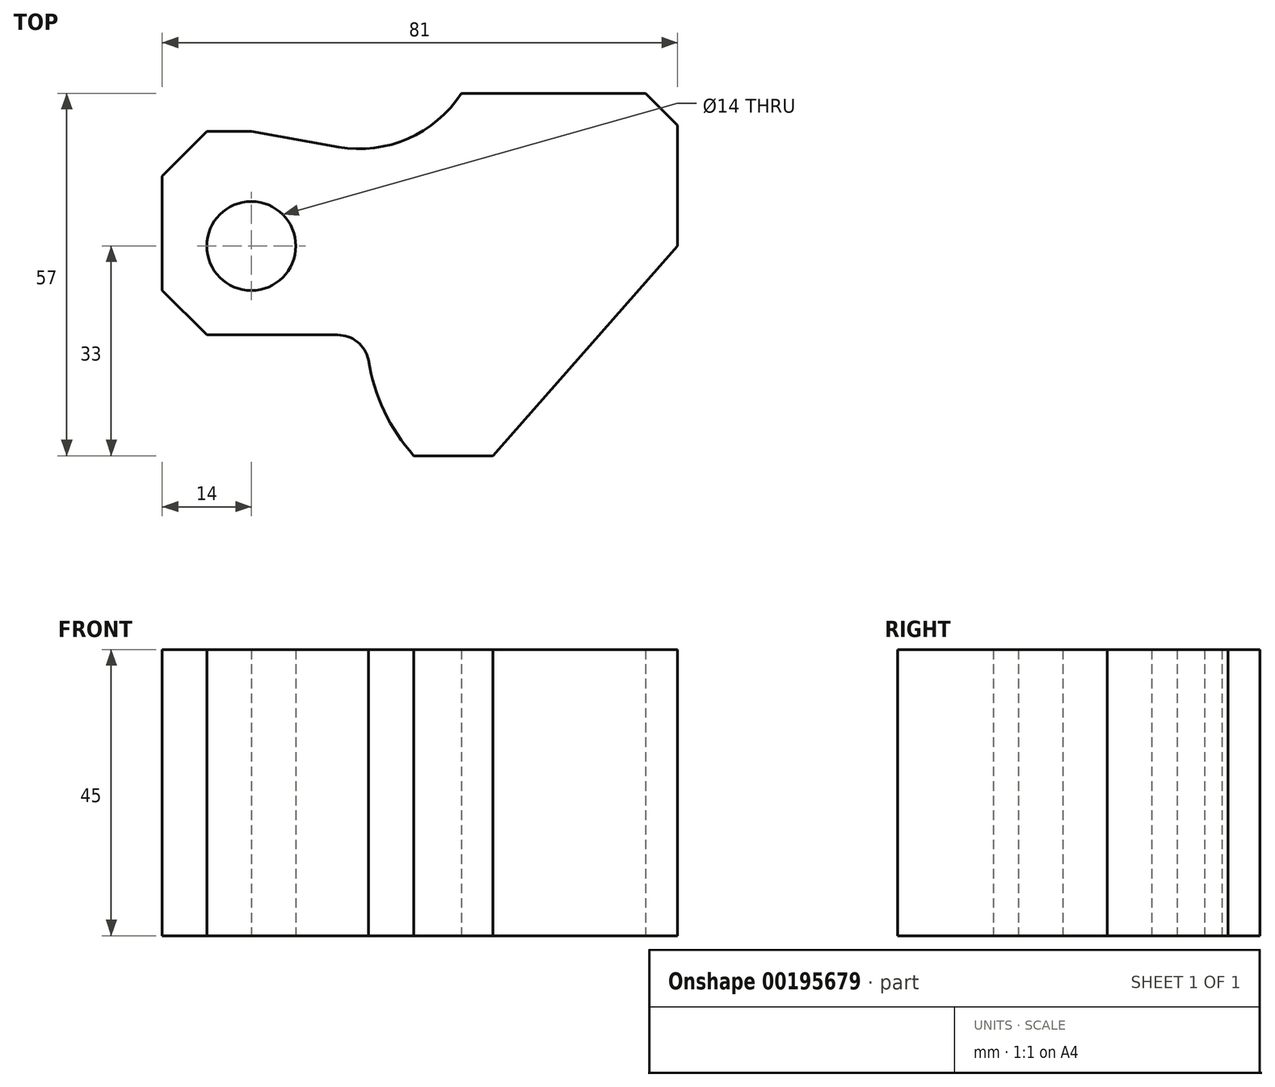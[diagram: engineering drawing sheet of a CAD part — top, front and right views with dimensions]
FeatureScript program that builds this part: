
annotation { "Feature Type Name" : "Feature", "Feature Type Description" : "" }
export const myFeature = defineFeature(function(context is Context, id is Id, definition is map)
    precondition{}
    {
        {
            var Q0;
            Q0=qCreatedBy(makeId("Top.planeOp"),FACE);
            var sketch = newSketch(context, id + "F0", { "sketchPlane" : qUnion([Q0])});
            skCircle(sketch, "E0", {"center": v(0, 0) * mm, "radius": 7 * mm});
            skLineSegment(sketch, "E1", {"start": v(-14, 11) * mm, "end": v(-7, 18) * mm});
            skLineSegment(sketch, "E2", {"start": v(-7, 18) * mm, "end": v(0, 18) * mm});
            skLineSegment(sketch, "E3", {"start": v(-14, 11) * mm, "end": v(-14, -7) * mm});
            skLineSegment(sketch, "E4", {"start": v(-14, -7) * mm, "end": v(-7, -14) * mm});
            skLineSegment(sketch, "E5", {"start": v(-7, -14) * mm, "end": v(13.55, -14) * mm});
            skArc(sketch, "E6", {"start": v(18.43, -17.93) * mm, "mid": v(20.9, -25.99) * mm, "end": v(25.57, -33) * mm});
            skLineSegment(sketch, "E7", {"start": v(0, 18) * mm, "end": v(13.73, 15.58) * mm});
            skArc(sketch, "E8", {"start": v(13.73, 15.58) * mm, "mid": v(24.64, 16.88) * mm, "end": v(33, 24) * mm});
            skArc(sketch, "E9", {"start": v(18.43, -17.93) * mm, "mid": v(16.68, -15.1) * mm, "end": v(13.55, -14) * mm});
            skLineSegment(sketch, "E10", {"start": v(25.57, -33) * mm, "end": v(38, -33) * mm});
            skLineSegment(sketch, "E11", {"start": v(38, -33) * mm, "end": v(67, 0) * mm});
            skLineSegment(sketch, "E12", {"start": v(33, 24) * mm, "end": v(62, 24) * mm});
            skLineSegment(sketch, "E13", {"start": v(62, 24) * mm, "end": v(67, 19) * mm});
            skLineSegment(sketch, "E14", {"start": v(67, 19) * mm, "end": v(67, 0) * mm});
            skSolve(sketch);
        }
        {
            var Q0;
            Q0 = qSketchRegion(id + "F0", true);
            extrude(context, id + "F1", {"entities" : qUnion([Q0]), "depth" : 45 * mm});
        }
    });
